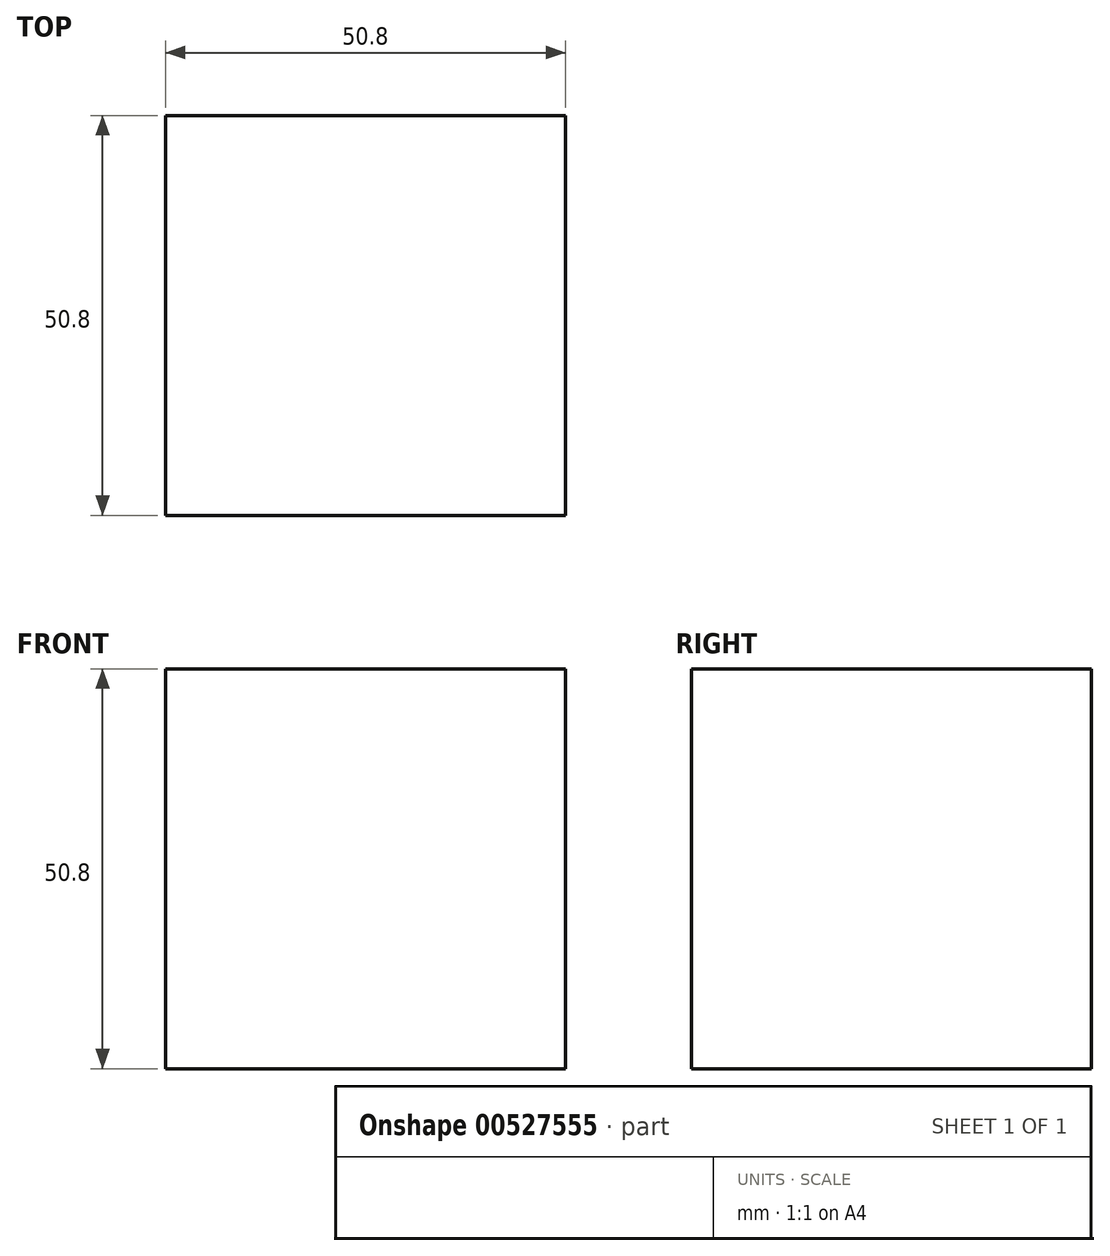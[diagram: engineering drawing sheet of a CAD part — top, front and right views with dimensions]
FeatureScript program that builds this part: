
annotation { "Feature Type Name" : "Feature", "Feature Type Description" : "" }
export const myFeature = defineFeature(function(context is Context, id is Id, definition is map)
    precondition{}
    {
        {
            var Q0;
            Q0=qCreatedBy(makeId("Front.planeOp"),FACE);
            var sketch = newSketch(context, id + "F0", { "sketchPlane" : qUnion([Q0])});
            skLineSegment(sketch, "E0", {"start": v(0, 0) * mm, "end": v(50.8, 0) * mm});
            skLineSegment(sketch, "E1", {"start": v(50.8, 0) * mm, "end": v(50.8, 50.8) * mm});
            skLineSegment(sketch, "E2", {"start": v(50.8, 50.8) * mm, "end": v(0, 50.8) * mm});
            skLineSegment(sketch, "E3", {"start": v(0, 50.8) * mm, "end": v(0, 0) * mm});
            skSolve(sketch);
        }
        {
            var Q0;
            Q0=makeQuery(id+"F0.imprint","IMPRINT",FACE,{"disambiguationData":[TD([[makeQuery(id+"F0.imprint","IMPRINT",EDGE,{"derivedFrom":sQuery(id+"F0.wireOp",EDGE,"E0")}),1.0]])]});
            extrude(context, id + "F1", {"entities" : qUnion([Q0]), "depth" : 50.8 * mm, "offsetDistance" : 25.4 * mm});
        }
    });
